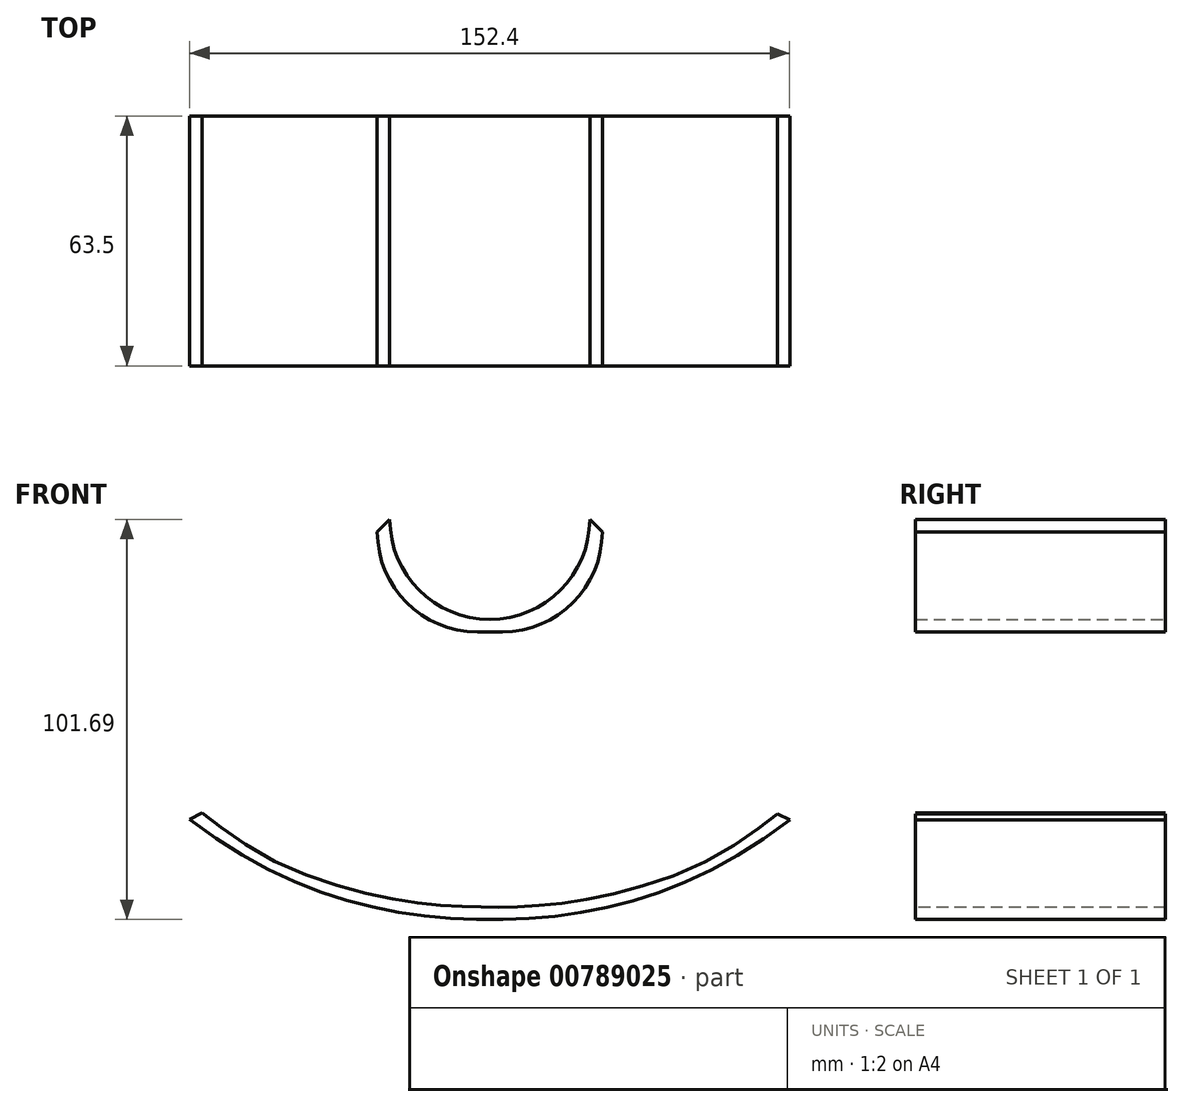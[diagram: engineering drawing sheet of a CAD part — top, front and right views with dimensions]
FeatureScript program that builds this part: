
annotation { "Feature Type Name" : "Feature", "Feature Type Description" : "" }
export const myFeature = defineFeature(function(context is Context, id is Id, definition is map)
    precondition{}
    {
        {
            var Q0;
            Q0=qCreatedBy(makeId("Front.planeOp"),FACE);
            var sketch = newSketch(context, id + "F0", { "sketchPlane" : qUnion([Q0])});
            skLineSegment(sketch, "E0.right", {"start": v(-52.68, 47.83) * mm, "end": v(-52.68, 47.83) * mm});
            skLineSegment(sketch, "E1.right", {"start": v(-1.88, 47.83) * mm, "end": v(-1.88, 47.83) * mm});
            skLineSegment(sketch, "E2", {"start": v(-27.28, 22.43) * mm, "end": v(-27.28, 22.43) * mm});
            skLineSegment(sketch, "E3", {"start": v(-78.08, -28.37) * mm, "end": v(23.52, -28.55) * mm, "construction": true});
            skFitSpline(sketch, "E4", {"points": [v(-103.48, -28.37) * mm, v(-27.28, -53.86) * mm, v(48.92, -28.55) * mm], "startDerivative": vector(152.37, -117.67) * mm, "endDerivative": vector(152.4, 117.72) * mm});
            skLineSegment(sketch, "E5", {"start": v(-27.28, -28.46) * mm, "end": v(-27.28, -53.86) * mm, "construction": true});
            skLineSegment(sketch, "E6", {"start": v(23.52, -28.55) * mm, "end": v(23.52, -48.17) * mm, "construction": true});
            skLineSegment(sketch, "E7", {"start": v(-78.08, -28.37) * mm, "end": v(-78.08, -47.98) * mm, "construction": true});
            skLineSegment(sketch, "E8.3", {"start": v(-55.85, 44.66) * mm, "end": v(-55.85, 44.66) * mm});
            skLineSegment(sketch, "E8.4", {"start": v(-30.45, 19.26) * mm, "end": v(-24.1, 19.26) * mm});
            skLineSegment(sketch, "E8.5", {"start": v(1.3, 44.66) * mm, "end": v(1.3, 44.66) * mm});
            skFitSpline(sketch, "E8.6", {"points": [v(-101.53, -25.86) * mm, v(-95.33, -30.65) * mm, v(-82.95, -38.52) * mm, v(-67.54, -44.76) * mm, v(-55.2, -47.98) * mm, v(-45.92, -49.59) * mm, v(-38.17, -50.34) * mm, v(-31.95, -50.63) * mm, v(-27.28, -50.7) * mm, v(-22.61, -50.65) * mm, v(-16.4, -50.38) * mm, v(-8.65, -49.66) * mm, v(0.63, -48.08) * mm, v(12.98, -44.9) * mm, v(28.4, -38.7) * mm, v(40.77, -30.83) * mm, v(46.98, -26.04) * mm]});
            skPoint(sketch, "E9.visualSharp", {"position": v(-52.68, 22.43) * mm});
            skArc(sketch, "E9.filletArc", {"start": v(-52.68, 47.83) * mm, "mid": v(-45.24, 29.87) * mm, "end": v(-27.28, 22.43) * mm});
            skPoint(sketch, "E10.visualSharp", {"position": v(-1.88, 22.43) * mm});
            skArc(sketch, "E10.filletArc", {"start": v(-27.28, 22.43) * mm, "mid": v(-9.31, 29.87) * mm, "end": v(-1.88, 47.83) * mm});
            skPoint(sketch, "E11.visualSharp", {"position": v(-55.85, 19.26) * mm});
            skArc(sketch, "E11.filletArc", {"start": v(-55.85, 44.66) * mm, "mid": v(-48.41, 26.7) * mm, "end": v(-30.45, 19.26) * mm});
            skPoint(sketch, "E12.visualSharp", {"position": v(1.3, 19.26) * mm});
            skArc(sketch, "E12.filletArc", {"start": v(-24.1, 19.26) * mm, "mid": v(-6.14, 26.7) * mm, "end": v(1.3, 44.66) * mm});
            skLineSegment(sketch, "E13", {"start": v(-55.85, 44.66) * mm, "end": v(-52.68, 47.83) * mm});
            skLineSegment(sketch, "E14", {"start": v(-1.88, 47.83) * mm, "end": v(1.3, 44.66) * mm});
            skLineSegment(sketch, "E15", {"start": v(-103.48, -28.37) * mm, "end": v(-100.3, -26.8) * mm});
            skLineSegment(sketch, "E16", {"start": v(48.92, -28.55) * mm, "end": v(45.75, -26.98) * mm});
            skSolve(sketch);
        }
        {
            var Q0;
            Q0=makeQuery(id+"F0.imprint","IMPRINT",FACE,{"disambiguationData":[TD([[makeQuery(id+"F0.imprint","IMPRINT",EDGE,{"derivedFrom":sQuery(id+"F0.wireOp",EDGE,"E8.4")}),1.0]])]});
            var Q1;
            Q1=makeQuery(id+"F0.imprint","IMPRINT",FACE,{"disambiguationData":[TD([[makeQuery(id+"F0.imprint","IMPRINT",EDGE,{"derivedFrom":sQuery(id+"F0.wireOp",EDGE,"E4")}),1.0]])]});
            extrude(context, id + "F1", {"entities" : qUnion([Q0, Q1]), "depth" : 63.5 * mm, "offsetDistance" : 25.4 * mm});
        }
    });
